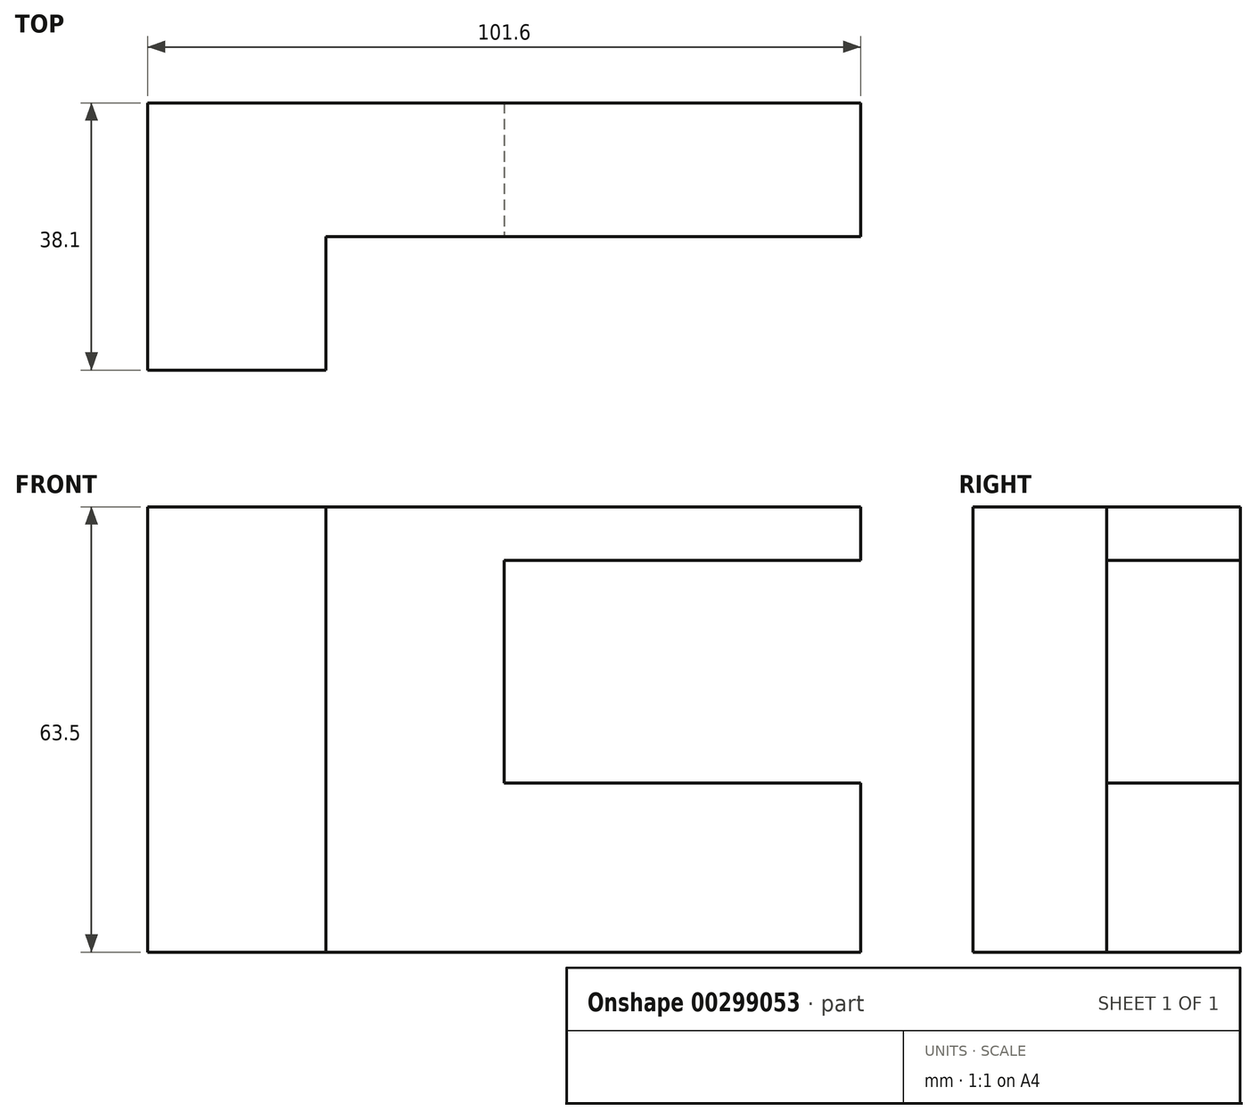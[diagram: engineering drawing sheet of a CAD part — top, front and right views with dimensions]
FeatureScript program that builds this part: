
annotation { "Feature Type Name" : "Feature", "Feature Type Description" : "" }
export const myFeature = defineFeature(function(context is Context, id is Id, definition is map)
    precondition{}
    {
        {
            var Q0;
            Q0=qCreatedBy(makeId("Front.planeOp"),FACE);
            var sketch = newSketch(context, id + "F0", { "sketchPlane" : qUnion([Q0])});
            skLineSegment(sketch, "E0.bottom", {"start": v(50.8, -31.75) * mm, "end": v(-50.8, -31.75) * mm});
            skLineSegment(sketch, "E0.top", {"start": v(50.8, 31.75) * mm, "end": v(-50.8, 31.75) * mm});
            skLineSegment(sketch, "E0.left", {"start": v(50.8, -31.75) * mm, "end": v(50.8, 31.75) * mm});
            skLineSegment(sketch, "E0.right", {"start": v(-50.8, -31.75) * mm, "end": v(-50.8, 31.75) * mm});
            skPoint(sketch, "E0.middle", {"position": v(0, 0) * mm});
            skSolve(sketch);
        }
        {
            var Q0;
            Q0 = qSketchRegion(id + "F0", true);
            extrude(context, id + "F1", {"entities" : qUnion([Q0]), "depth" : 38.1 * mm});
        }
        {
            var Q0;
            Q0=makeQuery(id+"F1.opExtrude","CAP_FACE",FACE,{"disambiguationData":[OSD([sQuery(id+"F0.wireOp",EDGE,"E0.bottom"),sQuery(id+"F0.wireOp",EDGE,"E0.top"),sQuery(id+"F0.wireOp",EDGE,"E0.left"),sQuery(id+"F0.wireOp",EDGE,"E0.right")])],"isStart":false});
            var sketch = newSketch(context, id + "F2", { "sketchPlane" : qUnion([Q0])});
            skLineSegment(sketch, "E1.bottom", {"start": v(-50.8, -31.75) * mm, "end": v(-25.4, -31.75) * mm});
            skLineSegment(sketch, "E1.top", {"start": v(-50.8, 31.75) * mm, "end": v(-25.4, 31.75) * mm});
            skLineSegment(sketch, "E1.left", {"start": v(-50.8, -31.75) * mm, "end": v(-50.8, 31.75) * mm});
            skLineSegment(sketch, "E1.right", {"start": v(-25.4, -31.75) * mm, "end": v(-25.4, 31.75) * mm});
            skLineSegment(sketch, "E2.bottom", {"start": v(-25.4, 31.75) * mm, "end": v(50.8, 31.75) * mm});
            skLineSegment(sketch, "E2.top", {"start": v(-25.4, -31.75) * mm, "end": v(50.8, -31.75) * mm});
            skLineSegment(sketch, "E2.left", {"start": v(-25.4, 31.75) * mm, "end": v(-25.4, -31.75) * mm});
            skLineSegment(sketch, "E2.right", {"start": v(50.8, 31.75) * mm, "end": v(50.8, -31.75) * mm});
            skSolve(sketch);
        }
        {
            var Q0;
            Q0=makeQuery(id+"F2.imprint","IMPRINT",FACE,{"disambiguationData":[TD([[makeQuery(id+"F2.imprint","IMPRINT",EDGE,{"derivedFrom":sQuery(id+"F2.wireOp",EDGE,"E2.bottom")}),1.0]])]});
            extrude(context, id + "F3", {"entities" : qUnion([Q0]), "operationType" : NewBodyOperationType.REMOVE, "oppositeDirection" : true, "depth" : 19.05 * mm});
        }
        {
            var Q0;
            Q0=makeQuery(id+"F3.boolean.opBoolean","COPY",FACE,{"derivedFrom":makeQuery(id+"F3.opExtrude","CAP_FACE",FACE,{"disambiguationData":[OSD([sQuery(id+"F2.wireOp",EDGE,"E2.bottom"),sQuery(id+"F2.wireOp",EDGE,"E2.top"),sQuery(id+"F2.wireOp",EDGE,"E2.left"),sQuery(id+"F2.wireOp",EDGE,"E2.right")])],"isStart":false})});
            var sketch = newSketch(context, id + "F4", { "sketchPlane" : qUnion([Q0])});
            skLineSegment(sketch, "E3.bottom", {"start": v(50.8, -7.65) * mm, "end": v(0, -7.65) * mm});
            skLineSegment(sketch, "E3.top", {"start": v(50.8, 24.1) * mm, "end": v(0, 24.1) * mm});
            skLineSegment(sketch, "E3.left", {"start": v(50.8, -7.65) * mm, "end": v(50.8, 24.1) * mm});
            skLineSegment(sketch, "E3.right", {"start": v(0, -7.65) * mm, "end": v(0, 24.1) * mm});
            skSolve(sketch);
        }
        {
            var Q0;
            Q0=makeQuery(id+"F4.imprint","IMPRINT",FACE,{"disambiguationData":[TD([[makeQuery(id+"F4.imprint","IMPRINT",EDGE,{"derivedFrom":sQuery(id+"F4.wireOp",EDGE,"E3.bottom")}),-1.0]])]});
            extrude(context, id + "F5", {"entities" : qUnion([Q0]), "operationType" : NewBodyOperationType.REMOVE, "oppositeDirection" : true, "depth" : 50.8 * mm});
        }
    });
